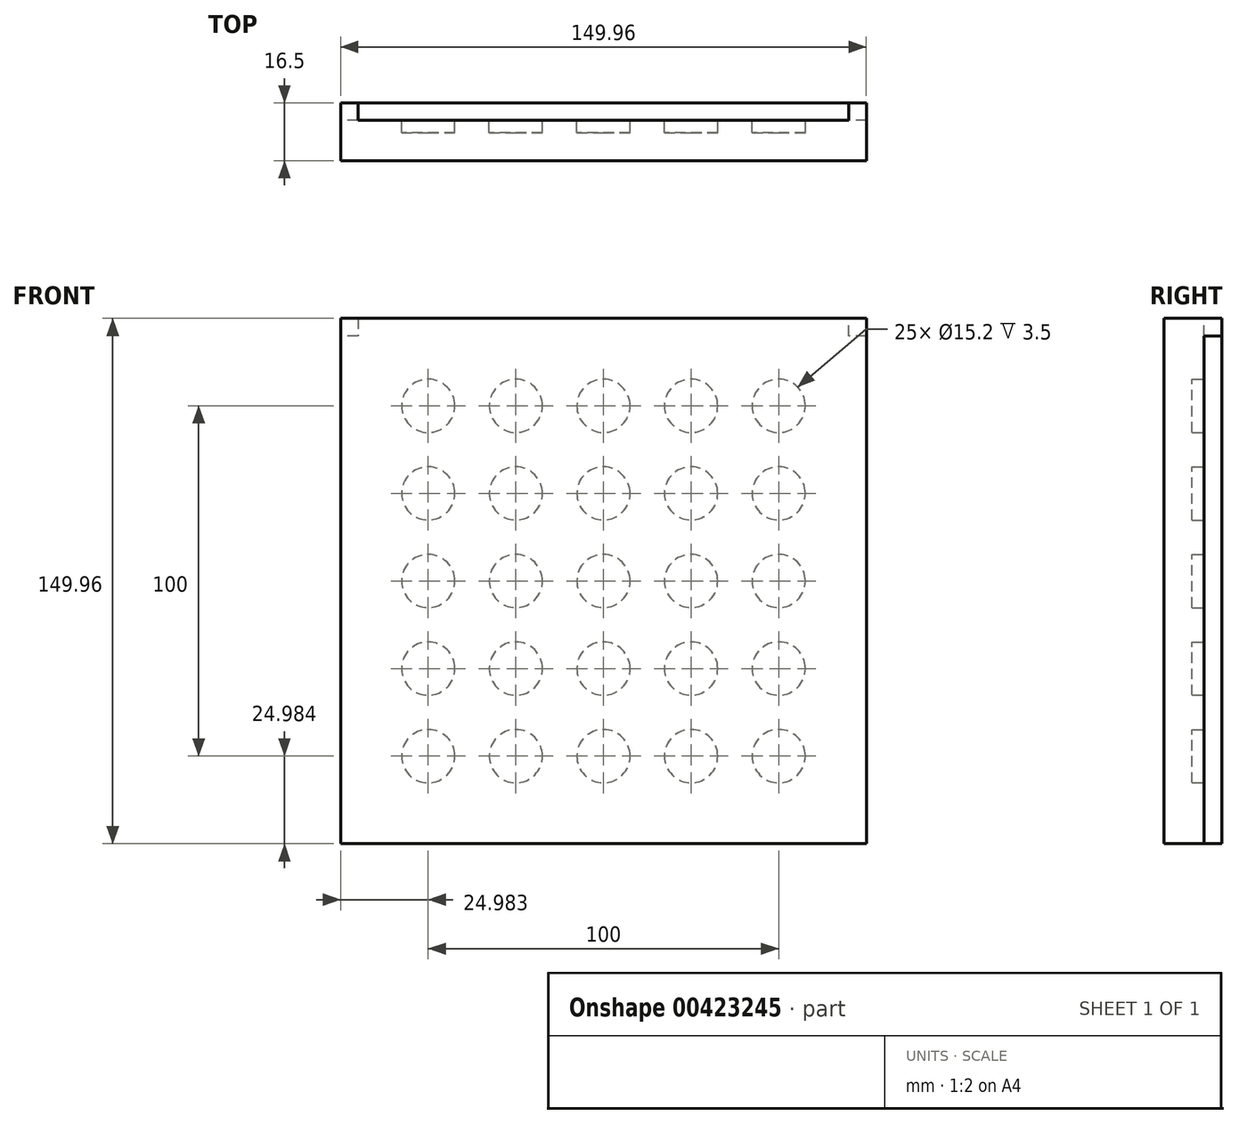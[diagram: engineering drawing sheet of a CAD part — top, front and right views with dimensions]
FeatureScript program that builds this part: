
annotation { "Feature Type Name" : "Feature", "Feature Type Description" : "" }
export const myFeature = defineFeature(function(context is Context, id is Id, definition is map)
    precondition{}
    {
        {
            var Q0;
            Q0=qCreatedBy(makeId("Front.planeOp"),FACE);
            var sketch = newSketch(context, id + "F0", { "sketchPlane" : qUnion([Q0])});
            skCircle(sketch, "E0", {"center": v(-61.1, 43.7) * mm, "radius": 7.6 * mm});
            skCircle(sketch, "E1.0.1.0", {"center": v(-61.1, 18.7) * mm, "radius": 7.6 * mm});
            skCircle(sketch, "E1.0.2.0", {"center": v(-61.1, -6.3) * mm, "radius": 7.6 * mm});
            skCircle(sketch, "E1.0.3.0", {"center": v(-61.1, -31.3) * mm, "radius": 7.6 * mm});
            skCircle(sketch, "E1.0.4.0", {"center": v(-61.1, -56.3) * mm, "radius": 7.6 * mm});
            skCircle(sketch, "E1.1.0.0", {"center": v(-36.1, 43.7) * mm, "radius": 7.6 * mm});
            skCircle(sketch, "E1.1.1.0", {"center": v(-36.1, 18.7) * mm, "radius": 7.6 * mm});
            skCircle(sketch, "E1.1.2.0", {"center": v(-36.1, -6.3) * mm, "radius": 7.6 * mm});
            skCircle(sketch, "E1.1.3.0", {"center": v(-36.1, -31.3) * mm, "radius": 7.6 * mm});
            skCircle(sketch, "E1.1.4.0", {"center": v(-36.1, -56.3) * mm, "radius": 7.6 * mm});
            skCircle(sketch, "E1.2.0.0", {"center": v(-11.1, 43.7) * mm, "radius": 7.6 * mm});
            skCircle(sketch, "E1.2.1.0", {"center": v(-11.1, 18.7) * mm, "radius": 7.6 * mm});
            skCircle(sketch, "E1.2.2.0", {"center": v(-11.1, -6.3) * mm, "radius": 7.6 * mm});
            skCircle(sketch, "E1.2.3.0", {"center": v(-11.1, -31.3) * mm, "radius": 7.6 * mm});
            skCircle(sketch, "E1.2.4.0", {"center": v(-11.1, -56.3) * mm, "radius": 7.6 * mm});
            skCircle(sketch, "E1.3.0.0", {"center": v(13.9, 43.7) * mm, "radius": 7.6 * mm});
            skCircle(sketch, "E1.3.1.0", {"center": v(13.9, 18.7) * mm, "radius": 7.6 * mm});
            skCircle(sketch, "E1.3.2.0", {"center": v(13.9, -6.3) * mm, "radius": 7.6 * mm});
            skCircle(sketch, "E1.3.3.0", {"center": v(13.9, -31.3) * mm, "radius": 7.6 * mm});
            skCircle(sketch, "E1.3.4.0", {"center": v(13.9, -56.3) * mm, "radius": 7.6 * mm});
            skCircle(sketch, "E1.4.0.0", {"center": v(38.9, 43.7) * mm, "radius": 7.6 * mm});
            skCircle(sketch, "E1.4.1.0", {"center": v(38.9, 18.7) * mm, "radius": 7.6 * mm});
            skCircle(sketch, "E1.4.2.0", {"center": v(38.9, -6.3) * mm, "radius": 7.6 * mm});
            skCircle(sketch, "E1.4.3.0", {"center": v(38.9, -31.3) * mm, "radius": 7.6 * mm});
            skCircle(sketch, "E1.4.4.0", {"center": v(38.9, -56.3) * mm, "radius": 7.6 * mm});
            skLineSegment(sketch, "E1.direction1", {"start": v(-61.1, 43.7) * mm, "end": v(-36.1, 43.7) * mm, "construction": true});
            skLineSegment(sketch, "E1.direction2", {"start": v(-61.1, 43.7) * mm, "end": v(-61.1, 18.7) * mm, "construction": true});
            skLineSegment(sketch, "E2", {"start": v(-11.1, -6.3) * mm, "end": v(-11.1, 100.02) * mm, "construction": true});
            skLineSegment(sketch, "E3", {"start": v(-11.1, -6.3) * mm, "end": v(76.39, -6.3) * mm, "construction": true});
            skLineSegment(sketch, "E4", {"start": v(58.88, 63.67) * mm, "end": v(-81.08, 63.67) * mm});
            skLineSegment(sketch, "E5", {"start": v(-81.08, 63.67) * mm, "end": v(-81.08, -76.29) * mm});
            skLineSegment(sketch, "E6", {"start": v(-81.08, -76.29) * mm, "end": v(58.88, -76.29) * mm});
            skLineSegment(sketch, "E7", {"start": v(58.88, 63.67) * mm, "end": v(58.88, -76.29) * mm});
            skSolve(sketch);
        }
        {
            var Q0;
            Q0=makeQuery(id+"F0.imprint","IMPRINT",FACE,{"disambiguationData":[TD([[makeQuery(id+"F0.imprint","IMPRINT",EDGE,{"derivedFrom":sQuery(id+"F0.wireOp",EDGE,"E0")}),-1.0]])]});
            extrude(context, id + "F1", {"entities" : qUnion([Q0]), "depth" : 3.5 * mm});
        }
        {
            var Q0;
            Q0=qCreatedBy(makeId("Front.planeOp"),FACE);
            cPlane(context, id + "F2", {"entities" : qUnion([Q0]), "cplaneType" : CPlaneType.OFFSET, "offset" : 3.5 * mm, "width" : 150 * mm, "height" : 150 * mm});
        }
        {
            var Q0;
            Q0=qCreatedBy(id+"F2.planeOp",FACE);
            var sketch = newSketch(context, id + "F3", { "sketchPlane" : qUnion([Q0])});
            skPoint(sketch, "E8.0", {"position": v(-81.08, 63.67) * mm});
            skPoint(sketch, "E9.0", {"position": v(58.88, 63.67) * mm});
            skPoint(sketch, "E10.0", {"position": v(58.88, -76.29) * mm});
            skPoint(sketch, "E11.0", {"position": v(-81.08, -76.29) * mm});
            skLineSegment(sketch, "E12", {"start": v(-81.08, 63.67) * mm, "end": v(58.88, 63.67) * mm});
            skLineSegment(sketch, "E13", {"start": v(58.88, 63.67) * mm, "end": v(58.88, -76.29) * mm});
            skLineSegment(sketch, "E14", {"start": v(58.88, -76.29) * mm, "end": v(-81.08, -76.29) * mm});
            skLineSegment(sketch, "E15", {"start": v(-81.08, -76.29) * mm, "end": v(-81.08, 63.67) * mm});
            skSolve(sketch);
        }
        {
            var Q0;
            Q0=makeQuery(id+"F3.imprint","IMPRINT",FACE,{"disambiguationData":[TD([[makeQuery(id+"F3.imprint","IMPRINT",EDGE,{"derivedFrom":sQuery(id+"F3.wireOp",EDGE,"E12")}),-1.0]])]});
            extrude(context, id + "F4", {"entities" : qUnion([Q0]), "depth" : 8 * mm});
        }
        {
            var Q0;
            Q0=makeQuery(id+"F4.opExtrude","CAP_FACE",FACE,{"disambiguationData":[OSD([sQuery(id+"F3.wireOp",EDGE,"E12"),sQuery(id+"F3.wireOp",EDGE,"E13"),sQuery(id+"F3.wireOp",EDGE,"E14"),sQuery(id+"F3.wireOp",EDGE,"E15")])],"isStart":false});
            cPlane(context, id + "F5", {"entities" : qUnion([Q0]), "cplaneType" : CPlaneType.OFFSET, "offset" : 0 * mm, "width" : 150 * mm, "height" : 150 * mm});
        }
        {
            var Q0;
            Q0=qCreatedBy(id+"F5.planeOp",FACE);
            var sketch = newSketch(context, id + "F6", { "sketchPlane" : qUnion([Q0])});
            skPoint(sketch, "E16.0", {"position": v(-81.08, 63.67) * mm});
            skPoint(sketch, "E17.0", {"position": v(58.88, 63.67) * mm});
            skPoint(sketch, "E18.0", {"position": v(58.88, -76.29) * mm});
            skPoint(sketch, "E19.0", {"position": v(-81.08, -76.29) * mm});
            skLineSegment(sketch, "E20", {"start": v(-81.08, 63.67) * mm, "end": v(58.88, 63.67) * mm});
            skLineSegment(sketch, "E21", {"start": v(58.88, 63.67) * mm, "end": v(58.88, -76.29) * mm});
            skLineSegment(sketch, "E22", {"start": v(58.88, -76.29) * mm, "end": v(63.88, -76.29) * mm});
            skLineSegment(sketch, "E23", {"start": v(63.88, -76.29) * mm, "end": v(63.88, 68.67) * mm});
            skLineSegment(sketch, "E24", {"start": v(63.88, 68.67) * mm, "end": v(-86.08, 68.67) * mm});
            skLineSegment(sketch, "E25", {"start": v(-86.08, 68.67) * mm, "end": v(-86.08, -76.29) * mm});
            skLineSegment(sketch, "E26", {"start": v(-86.08, -76.29) * mm, "end": v(-81.08, -76.29) * mm});
            skLineSegment(sketch, "E27", {"start": v(-81.08, -76.29) * mm, "end": v(-81.08, 63.67) * mm});
            skSolve(sketch);
        }
        {
            var Q0;
            Q0=makeQuery(id+"F6.imprint","IMPRINT",FACE,{"disambiguationData":[TD([[makeQuery(id+"F6.imprint","IMPRINT",EDGE,{"derivedFrom":sQuery(id+"F6.wireOp",EDGE,"E20")}),1.0]])]});
            extrude(context, id + "F7", {"entities" : qUnion([Q0]), "operationType" : NewBodyOperationType.ADD, "oppositeDirection" : true, "depth" : 11.5 * mm});
        }
        {
            var Q0;
            Q0=qCreatedBy(makeId("Front.planeOp"),FACE);
            var sketch = newSketch(context, id + "F8", { "sketchPlane" : qUnion([Q0])});
            skPoint(sketch, "E28.0", {"position": v(-86.08, -76.29) * mm});
            skPoint(sketch, "E29.0", {"position": v(63.88, -76.29) * mm});
            skLineSegment(sketch, "E30", {"start": v(-86.08, -76.29) * mm, "end": v(63.88, -76.29) * mm});
            skLineSegment(sketch, "E31", {"start": v(63.88, -76.29) * mm, "end": v(63.88, -81.29) * mm});
            skLineSegment(sketch, "E32", {"start": v(63.88, -81.29) * mm, "end": v(-86.08, -81.29) * mm});
            skLineSegment(sketch, "E33", {"start": v(-86.08, -81.29) * mm, "end": v(-86.08, -76.29) * mm});
            skSolve(sketch);
        }
        {
            var Q0;
            Q0=makeQuery(id+"F8.imprint","IMPRINT",FACE,{"disambiguationData":[TD([[makeQuery(id+"F8.imprint","IMPRINT",EDGE,{"derivedFrom":sQuery(id+"F8.wireOp",EDGE,"E30")}),-1.0]])]});
            extrude(context, id + "F9", {"entities" : qUnion([Q0]), "operationType" : NewBodyOperationType.ADD, "depth" : 11.5 * mm});
        }
        {
            var Q0;
            Q0=qCreatedBy(makeId("Front.planeOp"),FACE);
            var sketch = newSketch(context, id + "F10", { "sketchPlane" : qUnion([Q0])});
            skPoint(sketch, "E34.0", {"position": v(63.88, 68.67) * mm});
            skPoint(sketch, "E35.0", {"position": v(-86.08, 68.67) * mm});
            skPoint(sketch, "E36.0", {"position": v(-86.08, -81.29) * mm});
            skPoint(sketch, "E37.0", {"position": v(63.88, -81.29) * mm});
            skPoint(sketch, "E38.0", {"position": v(58.88, 63.67) * mm});
            skPoint(sketch, "E39.0", {"position": v(-81.08, 63.67) * mm});
            skLineSegment(sketch, "E40.bottom", {"start": v(63.88, 68.67) * mm, "end": v(58.88, 68.67) * mm});
            skLineSegment(sketch, "E40.top", {"start": v(63.88, 63.67) * mm, "end": v(58.88, 63.67) * mm});
            skLineSegment(sketch, "E40.left", {"start": v(63.88, 68.67) * mm, "end": v(63.88, 63.67) * mm});
            skLineSegment(sketch, "E40.right", {"start": v(58.88, 68.67) * mm, "end": v(58.88, 63.67) * mm});
            skLineSegment(sketch, "E41.bottom", {"start": v(-81.08, 63.67) * mm, "end": v(-86.08, 63.67) * mm});
            skLineSegment(sketch, "E41.top", {"start": v(-81.08, 68.67) * mm, "end": v(-86.08, 68.67) * mm});
            skLineSegment(sketch, "E41.left", {"start": v(-81.08, 63.67) * mm, "end": v(-81.08, 68.67) * mm});
            skLineSegment(sketch, "E41.right", {"start": v(-86.08, 63.67) * mm, "end": v(-86.08, 68.67) * mm});
            skSolve(sketch);
        }
        {
            var Q0;
            Q0=makeQuery(id+"F10.imprint","IMPRINT",FACE,{"disambiguationData":[TD([[makeQuery(id+"F10.imprint","IMPRINT",EDGE,{"derivedFrom":sQuery(id+"F10.wireOp",EDGE,"E41.bottom")}),-1.0]])]});
            var Q1;
            Q1=makeQuery(id+"F10.imprint","IMPRINT",FACE,{"disambiguationData":[TD([[makeQuery(id+"F10.imprint","IMPRINT",EDGE,{"derivedFrom":sQuery(id+"F10.wireOp",EDGE,"E40.bottom")}),1.0]])]});
            extrude(context, id + "F11", {"entities" : qUnion([Q0, Q1]), "operationType" : NewBodyOperationType.ADD, "oppositeDirection" : true, "depth" : 5 * mm});
        }
        {
            var Q0;
            Q0=qCreatedBy(makeId("Front.planeOp"),FACE);
            var sketch = newSketch(context, id + "F12", { "sketchPlane" : qUnion([Q0])});
            skPoint(sketch, "E42.0", {"position": v(63.88, 68.67) * mm});
            skPoint(sketch, "E43.0", {"position": v(58.88, 63.67) * mm});
            skPoint(sketch, "E44.0", {"position": v(58.88, 68.67) * mm});
            skPoint(sketch, "E45.0", {"position": v(63.88, 63.67) * mm});
            skPoint(sketch, "E46.0", {"position": v(-81.08, 68.67) * mm});
            skPoint(sketch, "E47.0", {"position": v(-81.08, 63.67) * mm});
            skPoint(sketch, "E48.0", {"position": v(-86.08, 63.67) * mm});
            skPoint(sketch, "E49.0", {"position": v(-86.08, -81.29) * mm});
            skPoint(sketch, "E50.0", {"position": v(63.88, -81.29) * mm});
            skLineSegment(sketch, "E51", {"start": v(58.88, 68.67) * mm, "end": v(-81.08, 68.67) * mm});
            skLineSegment(sketch, "E52", {"start": v(-81.08, 68.67) * mm, "end": v(-81.08, 63.67) * mm});
            skLineSegment(sketch, "E53", {"start": v(-81.08, 63.67) * mm, "end": v(-86.08, 63.67) * mm});
            skLineSegment(sketch, "E54", {"start": v(-86.08, 63.67) * mm, "end": v(-86.08, -81.29) * mm});
            skLineSegment(sketch, "E55", {"start": v(-86.08, -81.29) * mm, "end": v(63.88, -81.29) * mm});
            skLineSegment(sketch, "E56", {"start": v(63.88, -81.29) * mm, "end": v(63.88, 63.67) * mm});
            skLineSegment(sketch, "E57", {"start": v(63.88, 63.67) * mm, "end": v(58.88, 63.67) * mm});
            skLineSegment(sketch, "E58", {"start": v(58.88, 63.67) * mm, "end": v(58.88, 68.67) * mm});
            skSolve(sketch);
        }
        {
            var Q0;
            Q0 = qSketchRegion(id + "F12", true);
            extrude(context, id + "F13", {"entities" : qUnion([Q0]), "oppositeDirection" : true, "depth" : 5 * mm});
        }
    });
